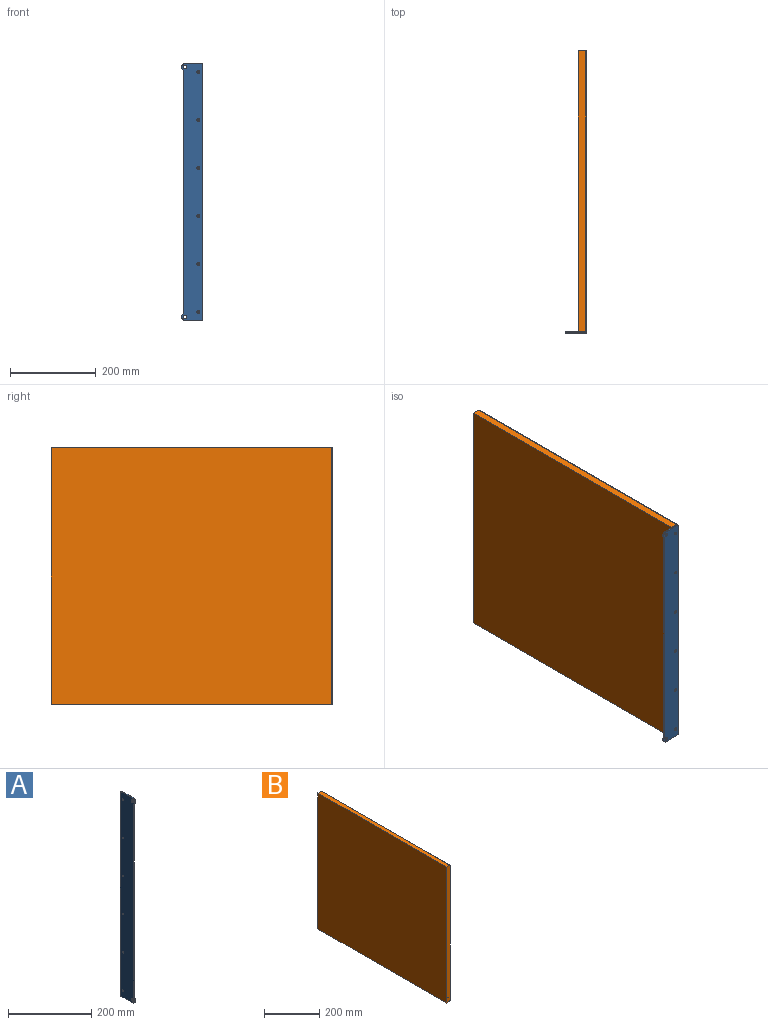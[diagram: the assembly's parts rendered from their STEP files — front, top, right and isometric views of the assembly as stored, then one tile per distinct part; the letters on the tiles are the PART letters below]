
ASSEMBLY  parts=2 mates=1
PART A: 24 faces, bbox 3x49x600 mm
  f0: cylinder r=8.5mm len=15.71mm, axis (-1,0,0), area 65.9mm2, adj f1,f7,f8,f9
  f1: plane 568.58x3mm, normal (0,-1,0), area 1705.7mm2, adj f0,f2,f8,f9
  f2: cylinder r=8.5mm len=15.71mm, axis (-1,0,0), area 65.9mm2, adj f1,f3,f8,f9
  f3: plane 38.5x3mm, normal (0,0,-1), area 115.5mm2, adj f2,f8,f9,f10
  f4: plane 596x3mm, normal (0,1,0), area 1788mm2, adj f8,f9,f10,f11
  f5: cylinder r=4mm len=8mm, axis (-1,0,0), area 75.4mm2, adj f8,f9
  f6: cylinder r=4mm len=8mm, axis (-1,0,0), area 75.4mm2, adj f8,f9
  f7: plane 38.5x3mm, normal (0,0,1), area 115.5mm2, adj f0,f8,f9,f11
  f8: plane 600x49mm, normal (1,0,0), area 26744.6mm2, adj f0,f1,f2,f3,f4,f5,f6,f7
  f9: plane 600x49mm, normal (-1,0,0), area 26900.1mm2, adj f0,f1,f2,f3,f4,f5,f6,f7
  f10: cylinder r=2mm len=3mm, axis (-1,0,0), area 9.4mm2, adj f3,f4,f8,f9
  f11: cylinder r=2mm len=3mm, axis (1,0,0), area 9.4mm2, adj f4,f7,f8,f9
  f12: cylinder r=2mm len=4mm, axis (1,0,0), area 18.8mm2, adj f9,f13
  f13: cone r=2mm half-angle=45deg, axis (1,0,0), area 36.7mm2, adj f8,f12
  f14: cylinder r=2mm len=4mm, axis (1,0,0), area 18.8mm2, adj f9,f15
  f15: cone r=2mm half-angle=45deg, axis (1,0,0), area 36.7mm2, adj f8,f14
  f16: cylinder r=2mm len=4mm, axis (1,0,0), area 18.8mm2, adj f9,f17
  f17: cone r=2mm half-angle=45deg, axis (1,0,0), area 36.7mm2, adj f8,f16
  f18: cylinder r=2mm len=4mm, axis (1,0,0), area 18.8mm2, adj f9,f19
  f19: cone r=2mm half-angle=45deg, axis (1,0,0), area 36.7mm2, adj f8,f18
  f20: cylinder r=2mm len=4mm, axis (1,0,0), area 18.8mm2, adj f9,f21
  f21: cone r=2mm half-angle=45deg, axis (1,0,0), area 36.7mm2, adj f8,f20
  f22: cylinder r=2mm len=4mm, axis (1,0,0), area 18.8mm2, adj f9,f23
  f23: cone r=2mm half-angle=45deg, axis (1,0,0), area 36.7mm2, adj f8,f22
PART B: 10 faces, bbox 19x655x600 mm
  f0: plane 655x17mm, normal (0,0,1), area 11135mm2, adj f1,f3,f5,f7
  f1: plane 600x19mm, normal (0,-1,0), area 11393.4mm2, adj f0,f2,f4,f5,f6,f7,f9
  f2: plane 655x17mm, normal (0,0,-1), area 11135mm2, adj f1,f3,f5,f6
  f3: plane 600x19mm, normal (0,1,0), area 11398.3mm2, adj f0,f2,f4,f5,f6,f7
  f4: plane 655x596mm, normal (1,0,0), area 390380mm2, adj f1,f3,f6,f7
  f5: plane 655x600mm, normal (-1,0,0), area 393000mm2, adj f0,f1,f2,f3
  f6: cylinder r=2mm len=655mm, axis (0,-1,0), area 2057.7mm2, adj f1,f2,f3,f4
  f7: cylinder r=2mm len=655mm, axis (0,1,0), area 2057.7mm2, adj f0,f1,f3,f4
  f8: cone r=0mm half-angle=59deg, axis (0,-1,0), area 5.7mm2, adj f9
  f9: cylinder r=1.25mm len=40mm, axis (0,-1,0), area 314.2mm2, adj f1,f8
PLACE A rot(axis=(0,0,-1),90deg) t=(183.19,-213.54,-66.26)mm
PLACE B t=(119.71,123.59,112.33)mm
MATE fastened B.f8 <-> A.f12  axis (0,-1,0) through (129.21,-213.54,-96.45)mm
